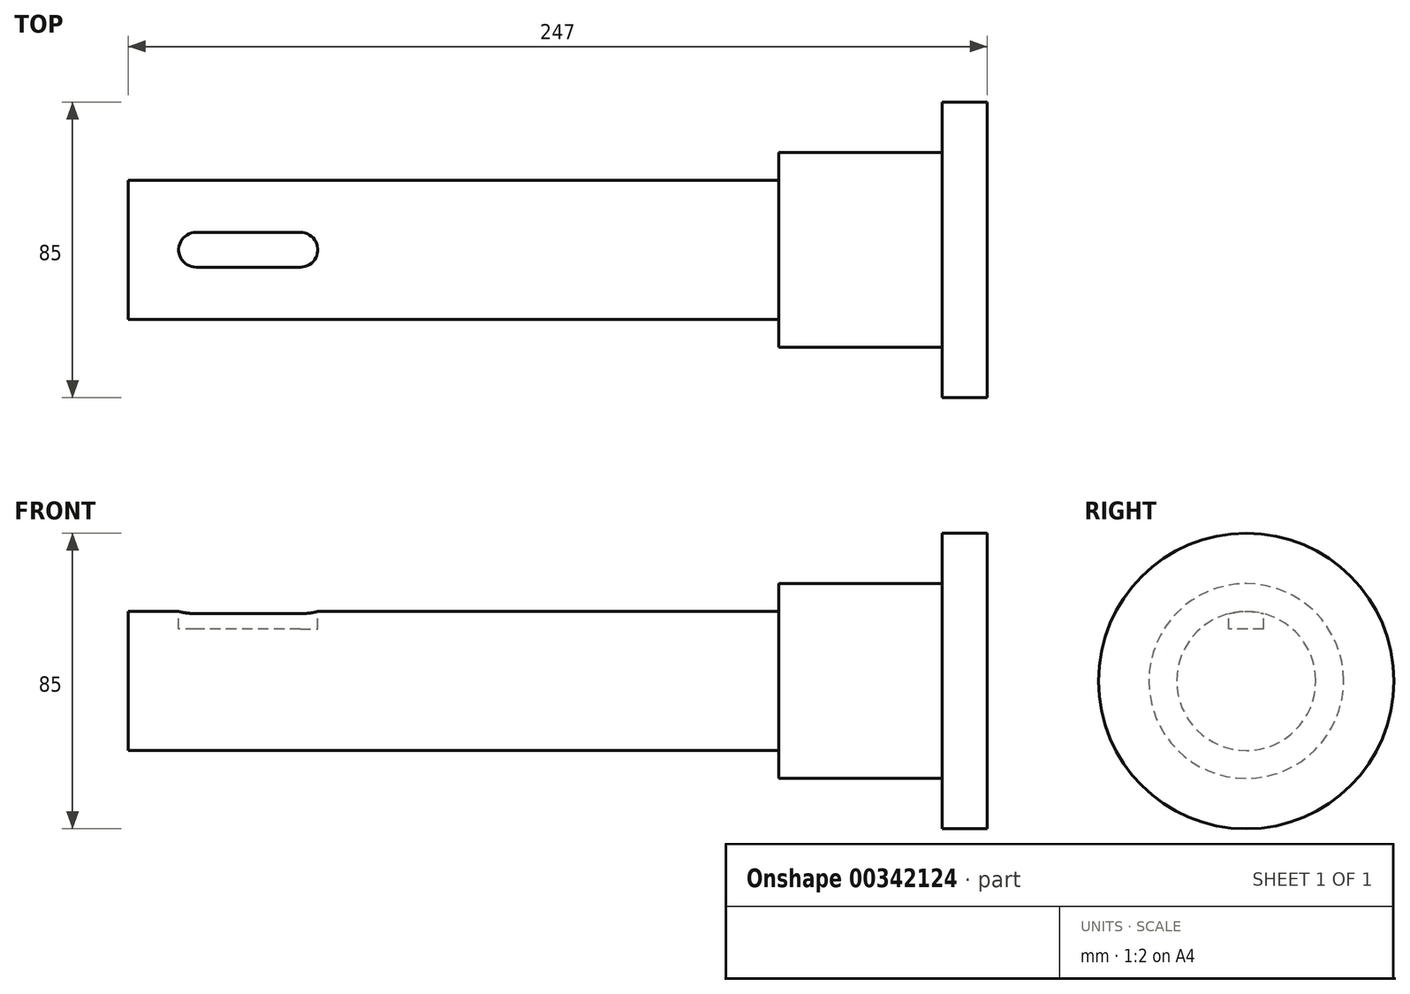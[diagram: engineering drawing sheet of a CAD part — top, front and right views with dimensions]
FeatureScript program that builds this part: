
annotation { "Feature Type Name" : "Feature", "Feature Type Description" : "" }
export const myFeature = defineFeature(function(context is Context, id is Id, definition is map)
    precondition{}
    {
        {
            var Q0;
            Q0=qCreatedBy(makeId("Front.planeOp"),FACE);
            var sketch = newSketch(context, id + "F0", { "sketchPlane" : qUnion([Q0])});
            skLineSegment(sketch, "E0.bottom", {"start": v(0, 0) * mm, "end": v(-187, 0) * mm});
            skLineSegment(sketch, "E0.top", {"start": v(0, 20) * mm, "end": v(-187, 20) * mm});
            skLineSegment(sketch, "E0.left", {"start": v(0, 0) * mm, "end": v(0, 20) * mm});
            skLineSegment(sketch, "E0.right", {"start": v(-187, 0) * mm, "end": v(-187, 20) * mm});
            skLineSegment(sketch, "E1.bottom", {"start": v(0, 0) * mm, "end": v(47, 0) * mm});
            skLineSegment(sketch, "E1.top", {"start": v(0, 28) * mm, "end": v(47, 28) * mm});
            skLineSegment(sketch, "E1.left", {"start": v(0, 0) * mm, "end": v(0, 28) * mm});
            skLineSegment(sketch, "E1.right", {"start": v(47, 0) * mm, "end": v(47, 28) * mm});
            skLineSegment(sketch, "E2.bottom", {"start": v(47, 0) * mm, "end": v(60, 0) * mm});
            skLineSegment(sketch, "E2.top", {"start": v(47, 42.5) * mm, "end": v(60, 42.5) * mm});
            skLineSegment(sketch, "E2.left", {"start": v(47, 0) * mm, "end": v(47, 42.5) * mm});
            skLineSegment(sketch, "E2.right", {"start": v(60, 0) * mm, "end": v(60, 42.5) * mm});
            skLineSegment(sketch, "E3", {"start": v(133.9, 0) * mm, "end": v(-297.9, 0) * mm});
            skSolve(sketch);
        }
        {
            var Q0;
            {var subQ3=sQuery(id+"F0.wireOp",EDGE,"E2.top");Q0=makeQuery(id+"F0.imprint","IMPRINT",FACE,{"disambiguationData":[TD([[makeQuery(id+"F0.imprint","IMPRINT",EDGE,{"derivedFrom":subQ3}),-1.0]])]});}
            var Q1;
            {var subQ0=sQuery(id+"F0.wireOp",EDGE,"E0.top");Q1=makeQuery(id+"F0.imprint","IMPRINT",FACE,{"disambiguationData":[TD([[makeQuery(id+"F0.imprint","IMPRINT",EDGE,{"derivedFrom":subQ0}),1.0]])]});}
            var Q2;
            {var subQ1=sQuery(id+"F0.wireOp",EDGE,"E1.top");Q2=makeQuery(id+"F0.imprint","IMPRINT",FACE,{"disambiguationData":[TD([[makeQuery(id+"F0.imprint","IMPRINT",EDGE,{"derivedFrom":subQ1}),-1.0]])]});}
            var Q3;
            Q3=sQuery(id+"F0.wireOp",EDGE,"E3");
            revolve(context, id + "F1", {"entities" : qUnion([Q0, Q1, Q2]), "axis" : qUnion([Q3]), "revolveType" : RevolveType.FULL});
        }
        {
            var Q0;
            Q0=qCreatedBy(makeId("Top.planeOp"),FACE);
            var sketch = newSketch(context, id + "F2", { "sketchPlane" : qUnion([Q0])});
            skLineSegment(sketch, "E4", {"start": v(-187, 20) * mm, "end": v(0, 20) * mm});
            skLineSegment(sketch, "E5.0", {"start": v(-187, 20) * mm, "end": v(-187, -20) * mm});
            skLineSegment(sketch, "E6", {"start": v(0, -20) * mm, "end": v(-187, -20) * mm});
            skLineSegment(sketch, "E7", {"start": v(47, -28) * mm, "end": v(0, -28) * mm});
            skLineSegment(sketch, "E8", {"start": v(0, 28) * mm, "end": v(47, 28) * mm});
            skLineSegment(sketch, "E9.0", {"start": v(47, 42.5) * mm, "end": v(47, -42.5) * mm});
            skLineSegment(sketch, "E10", {"start": v(47, 42.5) * mm, "end": v(60, 42.5) * mm});
            skLineSegment(sketch, "E11", {"start": v(60, -42.5) * mm, "end": v(47, -42.5) * mm});
            skLineSegment(sketch, "E12", {"start": v(-187, 0) * mm, "end": v(-167.5, 0) * mm});
            skCircle(sketch, "E13", {"center": v(-167.5, 0) * mm, "radius": 5 * mm});
            skLineSegment(sketch, "E14", {"start": v(-167.5, 0) * mm, "end": v(-137.5, 0) * mm});
            skCircle(sketch, "E15", {"center": v(-137.5, 0) * mm, "radius": 5 * mm});
            skLineSegment(sketch, "E16", {"start": v(-137.5, 0) * mm, "end": v(-137.5, 5) * mm});
            skLineSegment(sketch, "E17", {"start": v(-137.5, 5) * mm, "end": v(-167.5, 5) * mm});
            skLineSegment(sketch, "E18", {"start": v(-137.5, 0) * mm, "end": v(-137.5, -5) * mm});
            skLineSegment(sketch, "E19", {"start": v(-137.5, -5) * mm, "end": v(-167.5, -5) * mm});
            skSolve(sketch);
        }
        {
            var Q0;
            Q0=qSketchRegion(id+"F2",true);
            extrude(context, id + "F3", {"entities" : qUnion([Q0]), "operationType" : NewBodyOperationType.ADD, "depth" : 100 * mm});
        }
        {
            var Q0;
            Q0=makeQuery(id+"F3.opExtrude","CAP_FACE",FACE,{"disambiguationData":[OSD([sQuery(id+"F2.wireOp",EDGE,"E13"),sQuery(id+"F2.wireOp",EDGE,"E15"),sQuery(id+"F2.wireOp",EDGE,"E17"),sQuery(id+"F2.wireOp",EDGE,"E19")])],"isStart":false});
            extrude(context, id + "F4", {"entities" : qUnion([Q0]), "operationType" : NewBodyOperationType.REMOVE, "oppositeDirection" : true, "depth" : 85 * mm});
        }
    });
